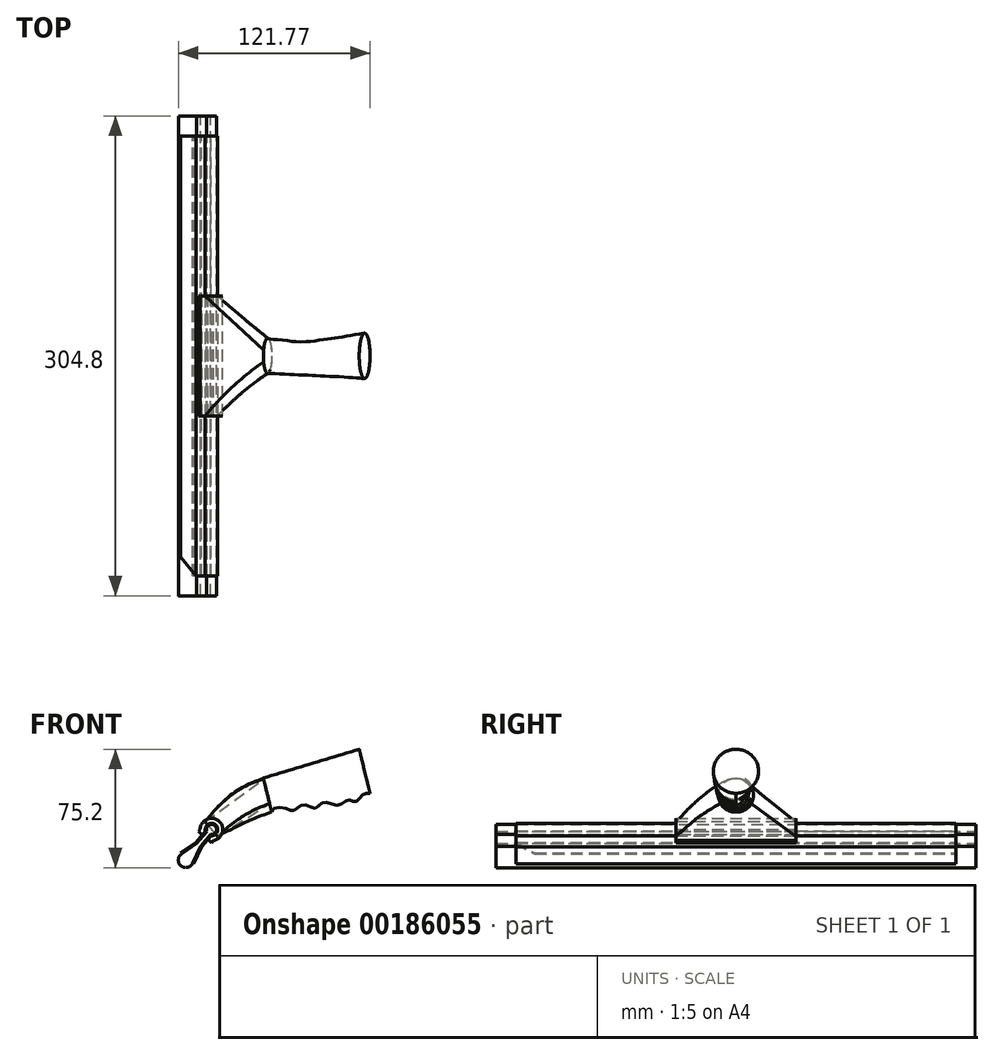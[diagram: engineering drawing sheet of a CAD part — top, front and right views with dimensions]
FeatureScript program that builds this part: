
annotation { "Feature Type Name" : "Feature", "Feature Type Description" : "" }
export const myFeature = defineFeature(function(context is Context, id is Id, definition is map)
    precondition{}
    {
        {
            var Q0;
            Q0=qCreatedBy(makeId("Front.planeOp"),FACE);
            var sketch = newSketch(context, id + "F0", { "sketchPlane" : qUnion([Q0])});
            skCircle(sketch, "E0", {"center": v(0, 0) * mm, "radius": 3.18 * mm});
            skCircle(sketch, "E1", {"center": v(-25.4, 0) * mm, "radius": 4.76 * mm});
            skLineSegment(sketch, "E2", {"start": v(-2.76, 1.57) * mm, "end": v(-12.7, 1.57) * mm});
            skLineSegment(sketch, "E3", {"start": v(-12.7, 1.57) * mm, "end": v(-24.19, 4.6) * mm});
            skLineSegment(sketch, "E4.MirrorCS", {"start": v(-2.76, -1.57) * mm, "end": v(-12.7, -1.57) * mm});
            skLineSegment(sketch, "E5.MirrorCS", {"start": v(-12.7, -1.57) * mm, "end": v(-24.19, -4.6) * mm});
            skSolve(sketch);
        }
        {
            var Q0;
            Q0 = qSketchRegion(id + "F0", true);
            extrude(context, id + "F1", {"entities" : qUnion([Q0]), "depth" : 304.8 * mm, "symmetric" : true});
        }
        {
            var Q0;
            Q0=qCreatedBy(makeId("Front.planeOp"),FACE);
            var sketch = newSketch(context, id + "F2", { "sketchPlane" : qUnion([Q0])});
            skLineSegment(sketch, "E6.0", {"start": v(-12.7, 1.57) * mm, "end": v(-24.19, 4.6) * mm});
            skLineSegment(sketch, "E7.0", {"start": v(-2.76, 1.57) * mm, "end": v(-12.7, 1.57) * mm});
            skArc(sketch, "E8.0", {"start": v(-2.76, -1.57) * mm, "mid": v(3.18, 0) * mm, "end": v(-2.76, 1.57) * mm});
            skLineSegment(sketch, "E9.0", {"start": v(-2.76, -1.57) * mm, "end": v(-12.7, -1.57) * mm});
            skLineSegment(sketch, "E10.0", {"start": v(-12.7, -1.57) * mm, "end": v(-24.19, -4.6) * mm});
            skLineSegment(sketch, "E11.0", {"start": v(-12.6, 2.39) * mm, "end": v(-23.98, 5.4) * mm});
            skLineSegment(sketch, "E11.1", {"start": v(-12.6, -2.39) * mm, "end": v(-23.98, -5.4) * mm});
            skLineSegment(sketch, "E11.2", {"start": v(-3.2, -2.39) * mm, "end": v(-12.6, -2.39) * mm});
            skArc(sketch, "E11.3", {"start": v(-3.2, -2.39) * mm, "mid": v(3.99, 0) * mm, "end": v(-3.2, 2.39) * mm});
            skLineSegment(sketch, "E11.4", {"start": v(-3.2, 2.39) * mm, "end": v(-12.6, 2.39) * mm});
            skLineSegment(sketch, "E12", {"start": v(-24.19, 4.6) * mm, "end": v(-23.98, 5.4) * mm});
            skLineSegment(sketch, "E13", {"start": v(-23.98, -5.4) * mm, "end": v(-24.19, -4.6) * mm});
            skSolve(sketch);
        }
        {
            var Q0;
            Q0=makeQuery(id+"F2.imprint","IMPRINT",FACE,{"disambiguationData":[TD([[makeQuery(id+"F2.imprint","IMPRINT",EDGE,{"derivedFrom":sQuery(id+"F2.wireOp",EDGE,"E6.0")}),-1.0]])]});
            extrude(context, id + "F3", {"entities" : qUnion([Q0]), "depth" : 279.4 * mm, "symmetric" : true});
        }
        {
            var Q0;
            Q0=makeQuery(id+"F3.opExtrude","SWEPT_FACE",FACE,{"disambiguationData":[OSD([sQuery(id+"F2.wireOp",EDGE,"E11.0")])]});
            var sketch = newSketch(context, id + "F4", { "sketchPlane" : qUnion([Q0])});
            skLineSegment(sketch, "E14", {"start": v(-12.79, -139.7) * mm, "end": v(-24.56, -127.93) * mm});
            skLineSegment(sketch, "E15", {"start": v(-24.56, -127.93) * mm, "end": v(-24.56, -139.7) * mm});
            skLineSegment(sketch, "E16", {"start": v(-24.56, -139.7) * mm, "end": v(-12.79, -139.7) * mm});
            skSolve(sketch);
        }
        {
            var Q0;
            Q0=makeQuery(id+"F4.imprint","IMPRINT",FACE,{"disambiguationData":[TD([[makeQuery(id+"F4.imprint","IMPRINT",EDGE,{"derivedFrom":sQuery(id+"F4.wireOp",EDGE,"E14")}),1.0]])]});
            extrude(context, id + "F5", {"entities" : qUnion([Q0]), "operationType" : NewBodyOperationType.REMOVE, "oppositeDirection" : true, "depth" : 0.81 * mm});
        }
        {
            var Q0;
            Q0=qCreatedBy(makeId("Front.planeOp"),FACE);
            var sketch = newSketch(context, id + "F6", { "sketchPlane" : qUnion([Q0])});
            skArc(sketch, "E17.0", {"start": v(-3.2, -2.39) * mm, "mid": v(3.99, 0) * mm, "end": v(-3.2, 2.39) * mm});
            skLineSegment(sketch, "E18.0", {"start": v(-3.2, 2.39) * mm, "end": v(-6.35, 2.39) * mm});
            skLineSegment(sketch, "E19.0", {"start": v(-3.2, -2.39) * mm, "end": v(-6.35, -2.39) * mm});
            skLineSegment(sketch, "E20.0", {"start": v(-4.51, 5.56) * mm, "end": v(-6.35, 5.56) * mm});
            skArc(sketch, "E20.1", {"start": v(-4.51, -5.56) * mm, "mid": v(7.16, 0) * mm, "end": v(-4.51, 5.56) * mm});
            skLineSegment(sketch, "E20.2", {"start": v(-4.51, -5.56) * mm, "end": v(-6.35, -5.56) * mm});
            skLineSegment(sketch, "E21", {"start": v(-6.35, 2.39) * mm, "end": v(-6.35, 5.56) * mm});
            skLineSegment(sketch, "E22", {"start": v(-6.35, -2.39) * mm, "end": v(-6.35, -5.56) * mm});
            skPoint(sketch, "E23.orphan", {"position": v(-12.6, -2.39) * mm});
            skPoint(sketch, "E24.orphan", {"position": v(-12.6, 2.39) * mm});
            skSolve(sketch);
        }
        {
            var Q0;
            Q0 = qSketchRegion(id + "F6", true);
            extrude(context, id + "F7", {"entities" : qUnion([Q0]), "operationType" : NewBodyOperationType.ADD, "depth" : 76.2 * mm, "symmetric" : true});
        }
        {
            var Q0;
            Q0=qCreatedBy(makeId("Front.planeOp"),FACE);
            var sketch = newSketch(context, id + "F8", { "sketchPlane" : qUnion([Q0])});
            skLineSegment(sketch, "E25", {"start": v(31.4, 38.8) * mm, "end": v(43.22, -9.26) * mm, "construction": true});
            skSolve(sketch);
        }
        {
            var Q0;
            Q0=qCreatedBy(makeId("Right.planeOp"),FACE);
            var Q1;
            Q1=sQuery(id+"F8.wireOp",EDGE,"E25");
            cPlane(context, id + "F9", {"entities" : qUnion([Q0, Q1]), "cplaneType" : CPlaneType.LINE_ANGLE, "offset" : 25.4 * mm, "angle" : 0 * degree, "width" : 152.4 * mm, "height" : 152.4 * mm});
        }
        {
            var Q0;
            Q0=qCreatedBy(id+"F9.planeOp",FACE);
            cPlane(context, id + "F10", {"entities" : qUnion([Q0]), "cplaneType" : CPlaneType.OFFSET, "offset" : 63.5 * mm, "oppositeDirection" : true, "width" : 152.4 * mm, "height" : 152.4 * mm});
        }
        {
            var Q0;
            Q0=qCreatedBy(id+"F9.planeOp",FACE);
            var sketch = newSketch(context, id + "F11", { "sketchPlane" : qUnion([Q0])});
            skPoint(sketch, "E26", {"position": v(0, 23.81) * mm});
            skPoint(sketch, "E27", {"position": v(0, 1.59) * mm});
            skLineSegment(sketch, "E28", {"start": v(0, 12.7) * mm, "end": v(-3.8, 23.14) * mm, "construction": true});
            skLineSegment(sketch, "E29", {"start": v(0, 12.7) * mm, "end": v(3.8, 23.14) * mm, "construction": true});
            skLineSegment(sketch, "E30", {"start": v(0, 12.7) * mm, "end": v(0, 23.81) * mm, "construction": true});
            skLineSegment(sketch, "E31", {"start": v(0, 12.7) * mm, "end": v(-9.62, 7.14) * mm, "construction": true});
            skLineSegment(sketch, "E32", {"start": v(0, 12.7) * mm, "end": v(9.62, 7.14) * mm, "construction": true});
            skArc(sketch, "E33", {"start": v(-3.8, 23.14) * mm, "mid": v(-10.44, 16.5) * mm, "end": v(-9.62, 7.14) * mm});
            skArc(sketch, "E34", {"start": v(3.8, 23.14) * mm, "mid": v(0, 23.81) * mm, "end": v(-3.8, 23.14) * mm});
            skArc(sketch, "E35", {"start": v(9.62, 7.14) * mm, "mid": v(10.44, 16.5) * mm, "end": v(3.8, 23.14) * mm});
            skArc(sketch, "E36", {"start": v(-9.62, 7.14) * mm, "mid": v(0, 1.59) * mm, "end": v(9.62, 7.14) * mm});
            skSolve(sketch);
        }
        {
            var Q0;
            Q0=qCreatedBy(id+"F10.planeOp",FACE);
            var sketch = newSketch(context, id + "F12", { "sketchPlane" : qUnion([Q0])});
            skPoint(sketch, "E37", {"position": v(0, 27.11) * mm});
            skPoint(sketch, "E38", {"position": v(0, -1.71) * mm});
            skArc(sketch, "E39", {"start": v(0, 27.11) * mm, "mid": v(-14.41, 12.74) * mm, "end": v(-0.08, -1.71) * mm});
            skArc(sketch, "E40", {"start": v(-0.08, -1.71) * mm, "mid": v(14.41, 12.66) * mm, "end": v(0, 27.11) * mm});
            skSolve(sketch);
        }
        {
            var Q0;
            Q0=qCreatedBy(makeId("Front.planeOp"),FACE);
            var sketch = newSketch(context, id + "F13", { "sketchPlane" : qUnion([Q0])});
            skLineSegment(sketch, "E41", {"start": v(32.93, 32.62) * mm, "end": v(93.8, 50.98) * mm});
            skFitSpline(sketch, "E42", {"points": [v(38.23, 11.03) * mm, v(45.88, 13.7) * mm, v(52.41, 12.07) * mm, v(58.12, 15.79) * mm, v(65.72, 13.54) * mm, v(71.42, 17.34) * mm, v(80.4, 15.44) * mm, v(87.14, 18.8) * mm, v(91.46, 17.6) * mm, v(95.96, 22) * mm, v(100.68, 22.98) * mm], "startDerivative": vector(-19.35, 78.7) * mm, "endDerivative": vector(58.24, -1.55) * mm});
            skLineSegment(sketch, "E43", {"start": v(33.86, 9.96) * mm, "end": v(38.23, 11.03) * mm, "construction": true});
            skSolve(sketch);
        }
        {
            var Q0;
            Q0=makeQuery(id+"F12.imprint","IMPRINT",FACE,{"disambiguationData":[TD([[makeQuery(id+"F12.imprint","IMPRINT",EDGE,{"derivedFrom":sQuery(id+"F12.wireOp",EDGE,"E39")}),1.0]])]});
            var Q1;
            Q1=makeQuery(id+"F11.imprint","IMPRINT",FACE,{"disambiguationData":[TD([[makeQuery(id+"F11.imprint","IMPRINT",EDGE,{"derivedFrom":sQuery(id+"F11.wireOp",EDGE,"E33")}),1.0]])]});
            var Q2;
            Q2=sQuery(id+"F13.wireOp",EDGE,"E42");
            var Q3;
            Q3=sQuery(id+"F13.wireOp",EDGE,"E41");
            loft(context, id + "F14", {"addGuides" : true, "sheetProfilesArray" : [{ "sheetProfileEntities" : qUnion([Q0]) }, { "sheetProfileEntities" : qUnion([Q1]) }], "guidesArray" : [{ "guideEntities" : qUnion([Q2]), "guideDerivativeType" : LoftGuideDerivativeType.DEFAULT, "guideDerivativeMagnitude" : 1 }, { "guideEntities" : qUnion([Q3]), "guideDerivativeType" : LoftGuideDerivativeType.DEFAULT, "guideDerivativeMagnitude" : 1 }]});
        }
        {
            var Q0;
            Q0=makeQuery(id+"F3.opExtrude","SWEPT_BODY",BODY,{"disambiguationData":[OSD([sQuery(id+"F2.wireOp",EDGE,"E6.0"),sQuery(id+"F2.wireOp",EDGE,"E7.0"),sQuery(id+"F2.wireOp",EDGE,"E8.0"),sQuery(id+"F2.wireOp",EDGE,"E9.0"),sQuery(id+"F2.wireOp",EDGE,"E10.0"),sQuery(id+"F2.wireOp",EDGE,"E11.0"),sQuery(id+"F2.wireOp",EDGE,"E11.1"),sQuery(id+"F2.wireOp",EDGE,"E11.2"),sQuery(id+"F2.wireOp",EDGE,"E11.3"),sQuery(id+"F2.wireOp",EDGE,"E11.4"),sQuery(id+"F2.wireOp",EDGE,"E12"),sQuery(id+"F2.wireOp",EDGE,"E13")])]});
            var Q1;
            Q1=makeQuery(id+"F1.opExtrude","SWEPT_BODY",BODY,{"disambiguationData":[OSD([sQuery(id+"F0.wireOp",EDGE,"E0"),sQuery(id+"F0.wireOp",EDGE,"E1"),sQuery(id+"F0.wireOp",EDGE,"E2"),sQuery(id+"F0.wireOp",EDGE,"E3"),sQuery(id+"F0.wireOp",EDGE,"E4.MirrorCS"),sQuery(id+"F0.wireOp",EDGE,"E5.MirrorCS")])]});
            var Q2;
            {var subQ1=sQuery(id+"F2.wireOp",EDGE,"E11.3");Q2=makeQuery(id+"F7.boolean.opBoolean","SPLIT",FACE,{"disambiguationData":[TD([makeQuery(id+"F7.opExtrude","CAP_FACE",FACE,{"disambiguationData":[OSD([sQuery(id+"F6.wireOp",EDGE,"E17.0"),sQuery(id+"F6.wireOp",EDGE,"E18.0"),sQuery(id+"F6.wireOp",EDGE,"E19.0"),sQuery(id+"F6.wireOp",EDGE,"E20.0"),sQuery(id+"F6.wireOp",EDGE,"E20.1"),sQuery(id+"F6.wireOp",EDGE,"E20.2"),sQuery(id+"F6.wireOp",EDGE,"E21"),sQuery(id+"F6.wireOp",EDGE,"E22")])],"isStart":false})])],"derivedFrom":makeQuery(id+"F3.opExtrude","SWEPT_FACE",FACE,{"disambiguationData":[OSD([subQ1])]})});}
            transform(context, id + "F15", {"entities" : qUnion([Q0, Q1]), "transformType" : TransformType.ROTATION, "transformAxis" : qUnion([Q2]), "angle" : 310 * degree, "makeCopy" : false});
        }
        {
            var Q0;
            Q0=qCreatedBy(makeId("Right.planeOp"),FACE);
            var Q1;
            {var subQ1=sQuery(id+"F2.wireOp",EDGE,"E11.3");Q1=makeQuery(id+"F7.boolean.opBoolean","SPLIT",FACE,{"disambiguationData":[TD([makeQuery(id+"F7.opExtrude","CAP_FACE",FACE,{"disambiguationData":[OSD([sQuery(id+"F6.wireOp",EDGE,"E17.0"),sQuery(id+"F6.wireOp",EDGE,"E18.0"),sQuery(id+"F6.wireOp",EDGE,"E19.0"),sQuery(id+"F6.wireOp",EDGE,"E20.0"),sQuery(id+"F6.wireOp",EDGE,"E20.1"),sQuery(id+"F6.wireOp",EDGE,"E20.2"),sQuery(id+"F6.wireOp",EDGE,"E21"),sQuery(id+"F6.wireOp",EDGE,"E22")])],"isStart":false})])],"derivedFrom":makeQuery(id+"F3.opExtrude","SWEPT_FACE",FACE,{"disambiguationData":[OSD([subQ1])]})});}
            cPlane(context, id + "F16", {"entities" : qUnion([Q0, Q1]), "cplaneType" : CPlaneType.LINE_ANGLE, "offset" : 25.4 * mm, "angle" : 320 * degree, "width" : 152.4 * mm, "height" : 152.4 * mm});
        }
        {
            var Q0;
            Q0=qCreatedBy(id+"F16.planeOp",FACE);
            var sketch = newSketch(context, id + "F17", { "sketchPlane" : qUnion([Q0])});
            skLineSegment(sketch, "E44.bottom", {"start": v(-38.1, 6.26) * mm, "end": v(38.1, 6.26) * mm});
            skLineSegment(sketch, "E44.top", {"start": v(-38.1, -5.8) * mm, "end": v(38.1, -5.8) * mm});
            skLineSegment(sketch, "E44.left", {"start": v(-38.1, 6.26) * mm, "end": v(-38.1, -5.8) * mm});
            skLineSegment(sketch, "E45", {"start": v(38.1, 6.26) * mm, "end": v(38.1, -5.8) * mm});
            skSolve(sketch);
        }
        {
            var Q0;
            Q0=sQuery(id+"F17.wireOp",VERTEX,"E45.start");
            var Q1;
            Q1=sQuery(id+"F17.wireOp",VERTEX,"E45.end");
            var Q2;
            Q2=sQuery(id+"F11.wireOp",VERTEX,"E34.start");
            cPlane(context, id + "F18", {"entities" : qUnion([Q0, Q1, Q2]), "cplaneType" : CPlaneType.THREE_POINT, "offset" : 25.4 * mm, "width" : 152.4 * mm, "height" : 152.4 * mm});
        }
        {
            var Q0;
            Q0=qCreatedBy(id+"F18.planeOp",FACE);
            var sketch = newSketch(context, id + "F19", { "sketchPlane" : qUnion([Q0])});
            skFitSpline(sketch, "E46", {"points": [v(20.28, -12.18) * mm, v(-21.48, 27.17) * mm], "startDerivative": vector(-38.72, 59.21) * mm, "endDerivative": vector(-49.01, 23.57) * mm});
            skSolve(sketch);
        }
        {
            var Q0;
            Q0=sQuery(id+"F19.wireOp",EDGE,"E46");
            extrude(context, id + "F20", {"bodyType" : ExtendedToolBodyType.SURFACE, "surfaceEntities" : qUnion([Q0]), "oppositeDirection" : true, "depth" : 25.4 * mm});
        }
        {
            var Q0;
            Q0=sQuery(id+"F11.wireOp",VERTEX,"E36.end");
            var Q1;
            Q1=sQuery(id+"F17.wireOp",VERTEX,"E45.end");
            var Q2;
            Q2=sQuery(id+"F17.wireOp",VERTEX,"E45.start");
            cPlane(context, id + "F21", {"entities" : qUnion([Q0, Q1, Q2]), "cplaneType" : CPlaneType.THREE_POINT, "offset" : 25.4 * mm, "width" : 152.4 * mm, "height" : 152.4 * mm});
        }
        {
            var Q0;
            Q0=qCreatedBy(id+"F21.planeOp",FACE);
            var sketch = newSketch(context, id + "F22", { "sketchPlane" : qUnion([Q0])});
            skFitSpline(sketch, "E47", {"points": [v(-11.42, -20.27) * mm, v(25.78, 10.76) * mm], "startDerivative": vector(34.27, 40) * mm, "endDerivative": vector(42.82, 23.68) * mm});
            skSolve(sketch);
        }
        {
            var Q0;
            Q0=sQuery(id+"F22.wireOp",EDGE,"E47");
            extrude(context, id + "F23", {"bodyType" : ExtendedToolBodyType.SURFACE, "surfaceEntities" : qUnion([Q0]), "depth" : 25.4 * mm});
        }
        {
            var Q0;
            Q0 = qSketchRegion(id + "F17", true);
            var Q1;
            Q1=makeQuery(id+"F11.imprint","IMPRINT",FACE,{"disambiguationData":[TD([[makeQuery(id+"F11.imprint","IMPRINT",EDGE,{"derivedFrom":sQuery(id+"F11.wireOp",EDGE,"E33")}),1.0]])]});
            var Q2;
            Q2=makeQuery(id+"F20.opExtrude","CAP_EDGE",EDGE,{"disambiguationData":[OSD([sQuery(id+"F19.wireOp",EDGE,"E46")])],"isStart":true});
            var Q3;
            Q3=makeQuery(id+"F23.opExtrude","CAP_EDGE",EDGE,{"disambiguationData":[OSD([sQuery(id+"F22.wireOp",EDGE,"E47")])],"isStart":true});
            var Q4;
            Q4=makeQuery(id+"FOd0o4de6fVlcvD_4.1.F20.opExtrude","CAP_EDGE",EDGE,{"disambiguationData":[OSD([sQuery(id+"F19.wireOp",EDGE,"E46")])],"isStart":true});
            var Q5;
            Q5=makeQuery(id+"FcTZy5CWcFqJOid_6.1.F23.opExtrude","CAP_EDGE",EDGE,{"disambiguationData":[OSD([sQuery(id+"F22.wireOp",EDGE,"E47")])],"isStart":true});
            loft(context, id + "F24", {"addGuides" : true, "sheetProfilesArray" : [{ "sheetProfileEntities" : qUnion([Q0]) }, { "sheetProfileEntities" : qUnion([Q1]) }], "guidesArray" : [{ "guideEntities" : qUnion([Q2]), "guideDerivativeType" : LoftGuideDerivativeType.DEFAULT, "guideDerivativeMagnitude" : 1 }, { "guideEntities" : qUnion([Q3]), "guideDerivativeType" : LoftGuideDerivativeType.DEFAULT, "guideDerivativeMagnitude" : 1 }, { "guideEntities" : qUnion([Q4]), "guideDerivativeType" : LoftGuideDerivativeType.DEFAULT, "guideDerivativeMagnitude" : 1 }, { "guideEntities" : qUnion([Q5]), "guideDerivativeType" : LoftGuideDerivativeType.DEFAULT, "guideDerivativeMagnitude" : 1 }]});
        }
    });
